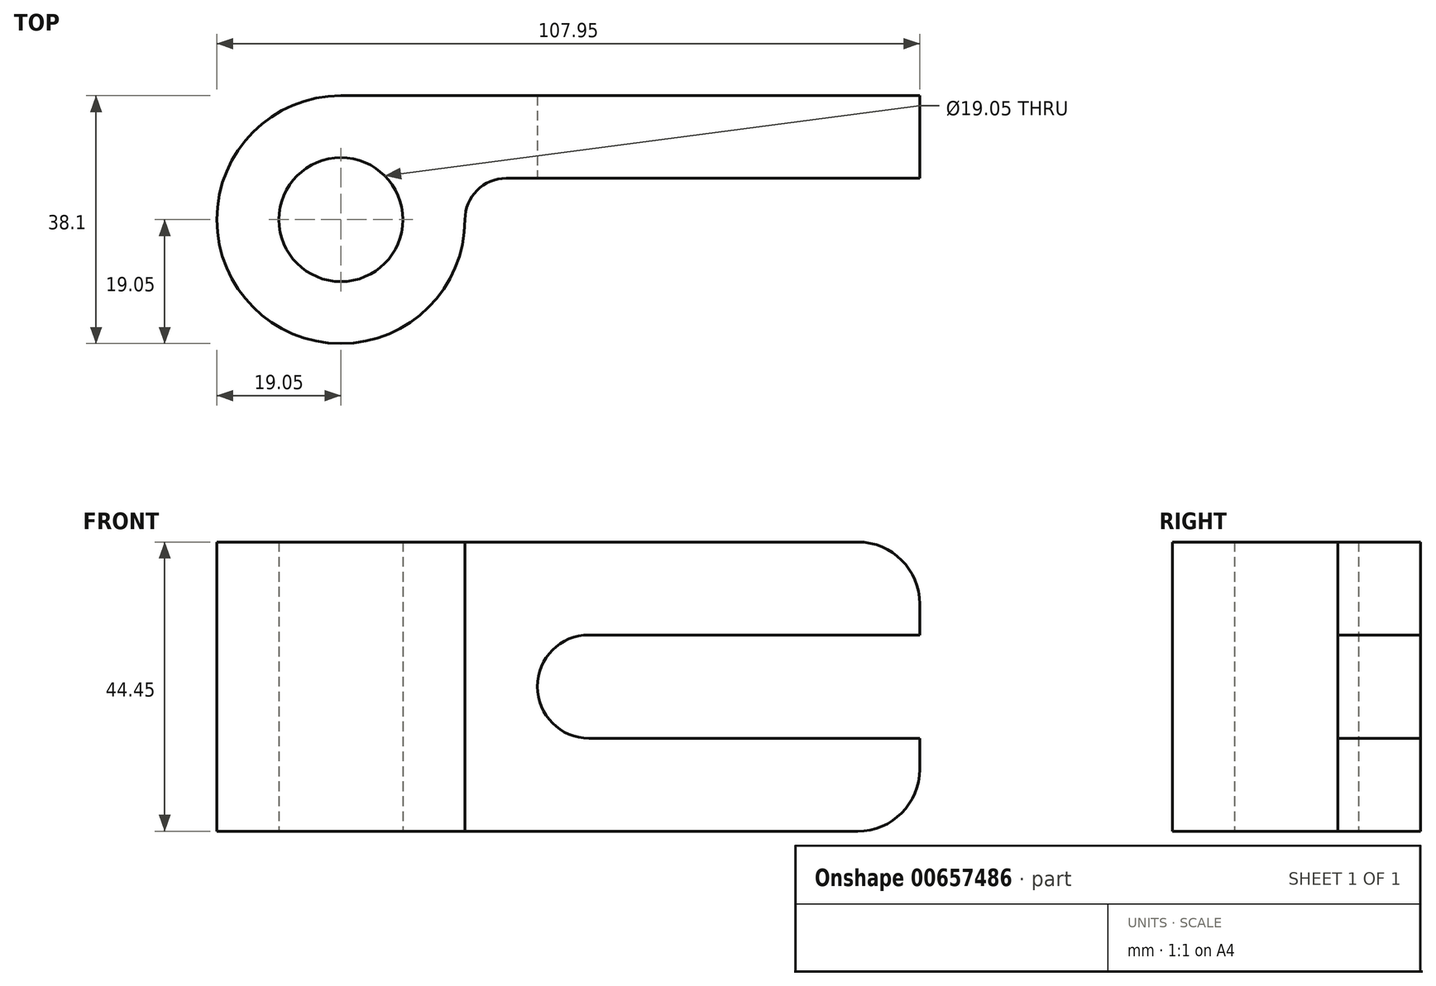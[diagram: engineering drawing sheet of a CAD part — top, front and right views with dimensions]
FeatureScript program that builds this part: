
annotation { "Feature Type Name" : "Feature", "Feature Type Description" : "" }
export const myFeature = defineFeature(function(context is Context, id is Id, definition is map)
    precondition{}
    {
        {
            var Q0;
            Q0=qCreatedBy(makeId("Top.planeOp"),FACE);
            var sketch = newSketch(context, id + "F0", { "sketchPlane" : qUnion([Q0])});
            skCircle(sketch, "E0", {"center": v(0, 0) * mm, "radius": 9.53 * mm});
            skArc(sketch, "E1", {"start": v(0, 19.05) * mm, "mid": v(-13.47, -13.47) * mm, "end": v(19.05, 0) * mm});
            skLineSegment(sketch, "E2", {"start": v(0, 19.05) * mm, "end": v(79.38, 19.05) * mm});
            skLineSegment(sketch, "E3", {"start": v(79.38, 19.05) * mm, "end": v(79.38, 6.35) * mm});
            skLineSegment(sketch, "E4", {"start": v(79.38, 6.35) * mm, "end": v(25.4, 6.35) * mm});
            skArc(sketch, "E5", {"start": v(25.4, 6.35) * mm, "mid": v(20.9, 4.5) * mm, "end": v(19.05, 0) * mm});
            skSolve(sketch);
        }
        {
            var Q0;
            Q0 = qSketchRegion(id + "F0", true);
            extrude(context, id + "F1", {"entities" : qUnion([Q0]), "depth" : 44.45 * mm, "offsetDistance" : 25.4 * mm});
        }
        {
            var Q0;
            Q0=makeQuery(id+"F1.opExtrude","SWEPT_FACE",FACE,{"disambiguationData":[OSD([sQuery(id+"F0.wireOp",EDGE,"E4")])]});
            var sketch = newSketch(context, id + "F2", { "sketchPlane" : qUnion([Q0])});
            skArc(sketch, "E6", {"start": v(88.9, 34.92) * mm, "mid": v(86.11, 41.66) * mm, "end": v(79.38, 44.45) * mm});
            skLineSegment(sketch, "E7", {"start": v(88.9, 34.92) * mm, "end": v(79.38, 34.92) * mm});
            skArc(sketch, "E8", {"start": v(79.38, 0) * mm, "mid": v(86.11, 2.79) * mm, "end": v(88.9, 9.53) * mm});
            skLineSegment(sketch, "E9", {"start": v(88.9, 9.53) * mm, "end": v(79.38, 9.53) * mm});
            skLineSegment(sketch, "E10", {"start": v(79.38, 44.45) * mm, "end": v(79.38, 34.93) * mm});
            skLineSegment(sketch, "E11", {"start": v(79.38, 9.53) * mm, "end": v(79.38, 0) * mm});
            skLineSegment(sketch, "E12", {"start": v(88.9, 34.92) * mm, "end": v(88.9, 30.16) * mm});
            skLineSegment(sketch, "E13", {"start": v(88.9, 30.16) * mm, "end": v(79.38, 30.16) * mm});
            skLineSegment(sketch, "E14", {"start": v(88.9, 9.53) * mm, "end": v(88.9, 14.29) * mm});
            skLineSegment(sketch, "E15", {"start": v(88.9, 14.29) * mm, "end": v(79.38, 14.29) * mm});
            skLineSegment(sketch, "E16", {"start": v(79.38, 34.93) * mm, "end": v(79.38, 30.16) * mm});
            skLineSegment(sketch, "E17", {"start": v(79.38, 14.29) * mm, "end": v(79.38, 9.53) * mm});
            skSolve(sketch);
        }
        {
            var Q0;
            Q0 = qSketchRegion(id + "F2", true);
            extrude(context, id + "F3", {"entities" : qUnion([Q0]), "operationType" : NewBodyOperationType.ADD, "oppositeDirection" : true, "depth" : 12.7 * mm, "offsetDistance" : 25.4 * mm});
        }
        {
            var Q0;
            Q0=makeQuery(id+"F3.boolean.opBoolean","MERGE",FACE,{"derivedFrom":[makeQuery(id+"F1.opExtrude","SWEPT_FACE",FACE,{"disambiguationData":[OSD([sQuery(id+"F0.wireOp",EDGE,"E4")])]}),makeQuery(id+"F3.opExtrude","CAP_FACE",FACE,{"disambiguationData":[OSD([sQuery(id+"F2.wireOp",EDGE,"E6"),sQuery(id+"F2.wireOp",EDGE,"E7"),sQuery(id+"F2.wireOp",EDGE,"E10")])],"isStart":true}),makeQuery(id+"F3.opExtrude","CAP_FACE",FACE,{"disambiguationData":[OSD([sQuery(id+"F2.wireOp",EDGE,"E8"),sQuery(id+"F2.wireOp",EDGE,"E9"),sQuery(id+"F2.wireOp",EDGE,"E11")])],"isStart":true})]});
            var sketch = newSketch(context, id + "F4", { "sketchPlane" : qUnion([Q0])});
            skArc(sketch, "E18", {"start": v(38.1, 30.16) * mm, "mid": v(30.16, 22.22) * mm, "end": v(38.1, 14.29) * mm});
            skPoint(sketch, "E18.first.point", {"position": v(30.2, 23.01) * mm});
            skPoint(sketch, "E18.second.point", {"position": v(38.1, 30.16) * mm});
            skPoint(sketch, "E18.third.point", {"position": v(38.1, 14.29) * mm});
            skLineSegment(sketch, "E19", {"start": v(38.1, 30.16) * mm, "end": v(79.38, 30.16) * mm});
            skLineSegment(sketch, "E20", {"start": v(79.38, 30.16) * mm, "end": v(79.38, 14.29) * mm});
            skLineSegment(sketch, "E21", {"start": v(79.38, 14.29) * mm, "end": v(38.1, 14.29) * mm});
            skPoint(sketch, "E22.end.orphan", {"position": v(88.9, 34.92) * mm});
            skPoint(sketch, "E23.start.orphan", {"position": v(88.9, 14.29) * mm});
            skPoint(sketch, "E24.orphan", {"position": v(84.14, 14.29) * mm});
            skSolve(sketch);
        }
        {
            var Q0;
            Q0 = qSketchRegion(id + "F4", true);
            extrude(context, id + "F5", {"entities" : qUnion([Q0]), "operationType" : NewBodyOperationType.REMOVE, "oppositeDirection" : true, "depth" : 12.7 * mm, "offsetDistance" : 25.4 * mm});
        }
    });
